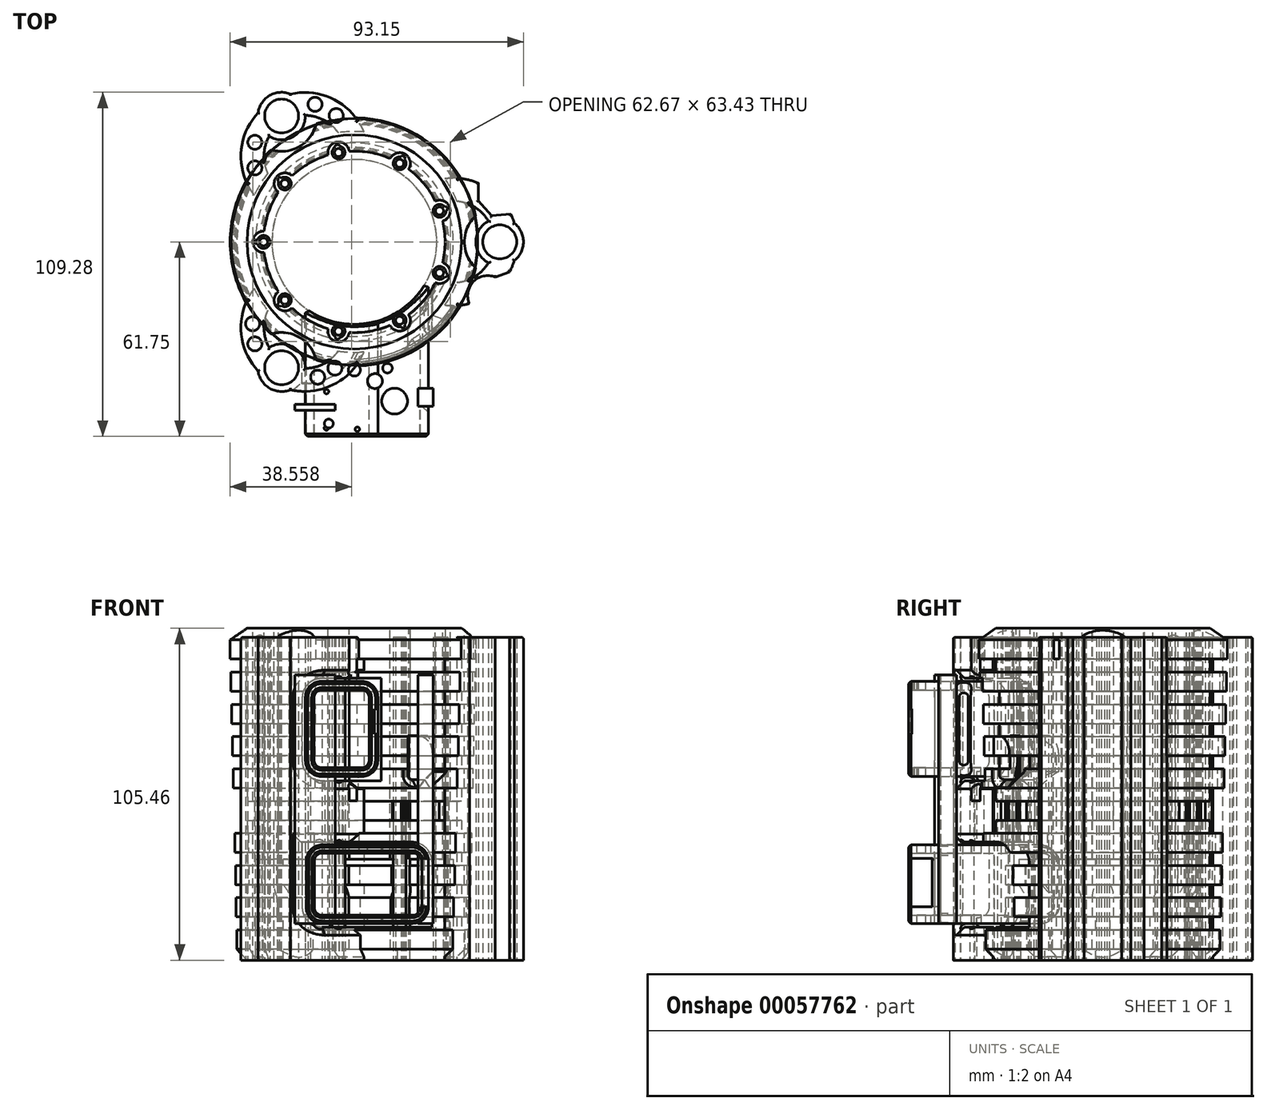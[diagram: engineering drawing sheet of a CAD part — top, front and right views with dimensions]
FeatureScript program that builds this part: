
annotation { "Feature Type Name" : "Feature", "Feature Type Description" : "" }
export const myFeature = defineFeature(function(context is Context, id is Id, definition is map)
    precondition{}
    {
        {
            var Q0;
            Q0=qCreatedBy(makeId("Front.planeOp"),FACE);
            var sketch = newSketch(context, id + "F0", { "sketchPlane" : qUnion([Q0])});
            skLineSegment(sketch, "E0.bottom", {"start": v(28.82, 39.62) * mm, "end": v(34.03, 39.62) * mm});
            skLineSegment(sketch, "E0.top", {"start": v(28.82, -33.71) * mm, "end": v(31.42, -33.71) * mm});
            skLineSegment(sketch, "E0.left", {"start": v(28.82, 39.62) * mm, "end": v(28.82, -33.71) * mm});
            skLineSegment(sketch, "E1.top", {"start": v(34.03, 29.82) * mm, "end": v(39.43, 29.82) * mm});
            skLineSegment(sketch, "E1.right", {"start": v(39.43, 35.92) * mm, "end": v(39.43, 29.82) * mm});
            skLineSegment(sketch, "E2.1.0.0", {"start": v(34.03, 25.68) * mm, "end": v(39.19, 25.68) * mm});
            skLineSegment(sketch, "E2.1.0.1", {"start": v(39.19, 25.68) * mm, "end": v(39.19, 19.58) * mm});
            skLineSegment(sketch, "E2.1.0.2", {"start": v(34.03, 19.58) * mm, "end": v(39.19, 19.58) * mm});
            skLineSegment(sketch, "E2.2.0.0", {"start": v(34.03, 15.44) * mm, "end": v(38.95, 15.44) * mm});
            skLineSegment(sketch, "E2.2.0.1", {"start": v(38.95, 15.44) * mm, "end": v(38.95, 9.34) * mm});
            skLineSegment(sketch, "E2.2.0.2", {"start": v(34.03, 9.34) * mm, "end": v(38.95, 9.34) * mm});
            skLineSegment(sketch, "E2.3.0.0", {"start": v(34.03, 5.2) * mm, "end": v(38.7, 5.2) * mm});
            skLineSegment(sketch, "E2.3.0.1", {"start": v(38.7, 5.2) * mm, "end": v(38.7, -0.9) * mm});
            skLineSegment(sketch, "E2.3.0.2", {"start": v(34.03, -0.9) * mm, "end": v(38.7, -0.9) * mm});
            skLineSegment(sketch, "E2.4.0.0", {"start": v(34.03, -5.04) * mm, "end": v(38.47, -5.04) * mm});
            skLineSegment(sketch, "E2.4.0.1", {"start": v(38.47, -5.04) * mm, "end": v(38.47, -11.14) * mm});
            skLineSegment(sketch, "E2.4.0.2", {"start": v(34.03, -11.14) * mm, "end": v(38.47, -11.14) * mm});
            skLineSegment(sketch, "E2.5.0.0", {"start": v(30.02, -15.28) * mm, "end": v(34.03, -15.28) * mm});
            skLineSegment(sketch, "E2.5.0.2", {"start": v(30.02, -21.38) * mm, "end": v(34.03, -21.38) * mm});
            skLineSegment(sketch, "E2.5.0.3", {"start": v(30.02, -15.28) * mm, "end": v(30.02, -21.38) * mm});
            skLineSegment(sketch, "E2.6.0.0", {"start": v(34.03, -25.52) * mm, "end": v(38, -25.52) * mm});
            skLineSegment(sketch, "E2.6.0.1", {"start": v(38, -25.52) * mm, "end": v(38, -31.62) * mm});
            skLineSegment(sketch, "E2.6.0.2", {"start": v(34.03, -31.62) * mm, "end": v(38, -31.62) * mm});
            skLineSegment(sketch, "E2.7.0.0", {"start": v(29.54, -35.76) * mm, "end": v(31.42, -35.76) * mm});
            skLineSegment(sketch, "E2.7.0.1", {"start": v(37.75, -35.76) * mm, "end": v(37.75, -41.86) * mm});
            skLineSegment(sketch, "E2.7.0.2", {"start": v(29.54, -41.86) * mm, "end": v(31.42, -41.86) * mm});
            skLineSegment(sketch, "E2.7.0.3", {"start": v(29.54, -35.76) * mm, "end": v(29.54, -41.86) * mm});
            skLineSegment(sketch, "E2.8.0.1", {"start": v(37.52, -46) * mm, "end": v(37.52, -52.1) * mm});
            skLineSegment(sketch, "E2.8.0.2", {"start": v(29.3, -52.1) * mm, "end": v(31.42, -52.1) * mm});
            skLineSegment(sketch, "E2.8.0.3", {"start": v(29.3, -46) * mm, "end": v(29.3, -52.1) * mm});
            skLineSegment(sketch, "E2.9.0.0", {"start": v(29.07, -56.24) * mm, "end": v(31.42, -56.24) * mm});
            skLineSegment(sketch, "E2.9.0.1", {"start": v(37.28, -56.24) * mm, "end": v(37.28, -62.34) * mm});
            skLineSegment(sketch, "E2.9.0.2", {"start": v(29.07, -62.34) * mm, "end": v(31.42, -62.34) * mm});
            skLineSegment(sketch, "E2.9.0.3", {"start": v(29.07, -56.24) * mm, "end": v(29.07, -62.34) * mm});
            skLineSegment(sketch, "E3", {"start": v(39.43, 35.92) * mm, "end": v(34.03, 39.62) * mm});
            skLineSegment(sketch, "E4.trimOffspring", {"start": v(34.03, 29.82) * mm, "end": v(34.03, 25.68) * mm});
            skLineSegment(sketch, "E5.trimOffspring", {"start": v(34.03, 19.58) * mm, "end": v(34.03, 15.44) * mm});
            skLineSegment(sketch, "E6.trimOffspring", {"start": v(34.03, 9.34) * mm, "end": v(34.03, 5.2) * mm});
            skLineSegment(sketch, "E7.trimOffspring", {"start": v(34.03, -0.9) * mm, "end": v(34.03, -5.04) * mm});
            skLineSegment(sketch, "E8.trimOffspring", {"start": v(34.03, -11.14) * mm, "end": v(34.03, -15.28) * mm});
            skLineSegment(sketch, "E9.trimOffspring", {"start": v(34.03, -21.38) * mm, "end": v(34.03, -25.52) * mm});
            skLineSegment(sketch, "E10.trimOffspring", {"start": v(34.03, -31.62) * mm, "end": v(34.03, -33.71) * mm});
            skPoint(sketch, "E11.firstSnap0", {"position": v(31.42, -33.71) * mm});
            skLineSegment(sketch, "E11.top", {"start": v(31.42, -65.84) * mm, "end": v(34.03, -65.84) * mm});
            skLineSegment(sketch, "E11.left", {"start": v(31.42, -33.71) * mm, "end": v(31.42, -35.76) * mm});
            skLineSegment(sketch, "E11.right", {"start": v(34.03, -31.62) * mm, "end": v(34.03, -35.76) * mm});
            skPoint(sketch, "E12.orphan", {"position": v(31.42, -31.62) * mm});
            skLineSegment(sketch, "E13.trimOffspring", {"start": v(34.03, -35.76) * mm, "end": v(37.75, -35.76) * mm});
            skLineSegment(sketch, "E14.trimOffspring", {"start": v(34.03, -41.86) * mm, "end": v(34.03, -46) * mm});
            skLineSegment(sketch, "E15.trimOffspring", {"start": v(31.42, -52.1) * mm, "end": v(31.42, -56.24) * mm});
            skLineSegment(sketch, "E16.trimOffspring", {"start": v(34.03, -52.1) * mm, "end": v(34.03, -56.24) * mm});
            skLineSegment(sketch, "E17.trimOffspring", {"start": v(31.42, -62.34) * mm, "end": v(31.42, -65.84) * mm});
            skLineSegment(sketch, "E18.trimOffspring", {"start": v(34.03, -56.24) * mm, "end": v(37.28, -56.24) * mm});
            skLineSegment(sketch, "E19.trimOffspring", {"start": v(34.03, -52.1) * mm, "end": v(37.52, -52.1) * mm});
            skLineSegment(sketch, "E20.trimOffspring", {"start": v(34.03, -46) * mm, "end": v(37.52, -46) * mm});
            skLineSegment(sketch, "E21.trimOffspring", {"start": v(34.03, -41.86) * mm, "end": v(37.75, -41.86) * mm});
            skLineSegment(sketch, "E22", {"start": v(34.03, -65.84) * mm, "end": v(37.28, -62.34) * mm});
            skLineSegment(sketch, "E23", {"start": v(29.3, -46) * mm, "end": v(31.42, -41.86) * mm});
            skPoint(sketch, "E24", {"position": v(0, 0) * mm});
            skLineSegment(sketch, "E25", {"start": v(0, 0) * mm, "end": v(0, 23.52) * mm});
            skSolve(sketch);
        }
        {
            var Q0;
            Q0=makeQuery(id+"F0.imprint","IMPRINT",FACE,{"disambiguationData":[TD([[makeQuery(id+"F0.imprint","IMPRINT",EDGE,{"derivedFrom":sQuery(id+"F0.wireOp",EDGE,"E0.bottom")}),-1.0]])]});
            var Q1;
            Q1=sQuery(id+"F0.wireOp",EDGE,"E25");
            revolve(context, id + "F1", {"entities" : qUnion([Q0]), "axis" : qUnion([Q1]), "revolveType" : RevolveType.FULL});
        }
        {
            var Q0;
            Q0=makeQuery(id+"F1.opRevolve","SWEPT_FACE",FACE,{"disambiguationData":[OSD([sQuery(id+"F0.wireOp",EDGE,"E0.bottom")])]});
            var sketch = newSketch(context, id + "F2", { "sketchPlane" : qUnion([Q0])});
            skCircle(sketch, "E26", {"center": v(46.18, 0) * mm, "radius": 11.2 * mm});
            skCircle(sketch, "E27.1.0", {"center": v(-23.09, 39.99) * mm, "radius": 11.2 * mm});
            skCircle(sketch, "E27.2.0", {"center": v(-23.09, -39.99) * mm, "radius": 11.2 * mm});
            skPoint(sketch, "E27.center", {"position": v(0, 0) * mm});
            skCircle(sketch, "E28", {"center": v(-28.82, 0) * mm, "radius": 3.4 * mm});
            skCircle(sketch, "E29.1.0", {"center": v(-22.07, -18.52) * mm, "radius": 3.4 * mm});
            skCircle(sketch, "E29.2.0", {"center": v(-5, -28.38) * mm, "radius": 3.4 * mm});
            skCircle(sketch, "E29.3.0", {"center": v(14.4, -24.95) * mm, "radius": 3.4 * mm});
            skCircle(sketch, "E29.4.0", {"center": v(27.08, -9.86) * mm, "radius": 3.4 * mm});
            skCircle(sketch, "E29.5.0", {"center": v(27.08, 9.86) * mm, "radius": 3.4 * mm});
            skCircle(sketch, "E29.6.0", {"center": v(14.4, 24.95) * mm, "radius": 3.4 * mm});
            skCircle(sketch, "E29.7.0", {"center": v(-5, 28.38) * mm, "radius": 3.4 * mm});
            skCircle(sketch, "E29.8.0", {"center": v(-22.07, 18.52) * mm, "radius": 3.4 * mm});
            skSolve(sketch);
        }
        {
            var Q0;
            Q0=makeQuery(id+"F1.opRevolve","SWEPT_FACE",FACE,{"disambiguationData":[OSD([sQuery(id+"F0.wireOp",EDGE,"E11.top")])]});
            var sketch = newSketch(context, id + "F3", { "sketchPlane" : qUnion([Q0])});
            skCircle(sketch, "E30", {"center": v(46.18, 0) * mm, "radius": 5.4 * mm});
            skPoint(sketch, "E31.center", {"position": v(0, 0) * mm});
            skArc(sketch, "E32", {"start": v(-30.81, -0.54) * mm, "mid": v(-26.75, -0.02) * mm, "end": v(-30.8, 0.58) * mm});
            skCircle(sketch, "E33.0", {"center": v(-28.82, 0) * mm, "radius": 1.27 * mm});
            skLineSegment(sketch, "E34.bottom", {"start": v(-30.8, 0.58) * mm, "end": v(-32.97, 0.58) * mm});
            skLineSegment(sketch, "E34.top", {"start": v(-30.81, -0.54) * mm, "end": v(-32.97, -0.54) * mm});
            skLineSegment(sketch, "E34.right", {"start": v(-32.97, 0.58) * mm, "end": v(-32.97, -0.54) * mm});
            skArc(sketch, "E35.1.0", {"start": v(-23.25, -20.22) * mm, "mid": v(-20.48, -17.2) * mm, "end": v(-23.97, -19.35) * mm});
            skLineSegment(sketch, "E35.1.1", {"start": v(-23.25, -20.22) * mm, "end": v(-24.9, -21.6) * mm});
            skLineSegment(sketch, "E35.1.2", {"start": v(-23.97, -19.35) * mm, "end": v(-25.63, -20.74) * mm});
            skCircle(sketch, "E35.1.3", {"center": v(-22.07, -18.52) * mm, "radius": 1.27 * mm});
            skLineSegment(sketch, "E35.1.4", {"start": v(-25.63, -20.74) * mm, "end": v(-24.9, -21.6) * mm});
            skArc(sketch, "E35.2.0", {"start": v(-4.82, -30.44) * mm, "mid": v(-4.62, -26.34) * mm, "end": v(-5.92, -30.23) * mm});
            skLineSegment(sketch, "E35.2.1", {"start": v(-4.82, -30.44) * mm, "end": v(-5.2, -32.56) * mm});
            skLineSegment(sketch, "E35.2.2", {"start": v(-5.92, -30.23) * mm, "end": v(-6.3, -32.36) * mm});
            skCircle(sketch, "E35.2.3", {"center": v(-5, -28.38) * mm, "radius": 1.27 * mm});
            skLineSegment(sketch, "E35.2.4", {"start": v(-6.3, -32.36) * mm, "end": v(-5.2, -32.56) * mm});
            skArc(sketch, "E36.2.3.0", {"start": v(15.87, -26.41) * mm, "mid": v(13.4, -23.15) * mm, "end": v(14.9, -26.96) * mm});
            skLineSegment(sketch, "E36.4.3.0", {"start": v(15.87, -26.41) * mm, "end": v(16.95, -28.28) * mm});
            skLineSegment(sketch, "E36.7.3.0", {"start": v(14.9, -26.96) * mm, "end": v(15.98, -28.84) * mm});
            skCircle(sketch, "E36.10.3.0", {"center": v(14.4, -24.95) * mm, "radius": 1.27 * mm});
            skLineSegment(sketch, "E36.12.3.0", {"start": v(15.98, -28.84) * mm, "end": v(16.95, -28.28) * mm});
            skArc(sketch, "E36.2.4.0", {"start": v(29.14, -10.03) * mm, "mid": v(25.14, -9.13) * mm, "end": v(28.74, -11.08) * mm});
            skLineSegment(sketch, "E36.4.4.0", {"start": v(29.14, -10.03) * mm, "end": v(31.16, -10.77) * mm});
            skLineSegment(sketch, "E36.7.4.0", {"start": v(28.74, -11.08) * mm, "end": v(30.78, -11.82) * mm});
            skCircle(sketch, "E36.10.4.0", {"center": v(27.08, -9.86) * mm, "radius": 1.27 * mm});
            skLineSegment(sketch, "E36.12.4.0", {"start": v(30.78, -11.82) * mm, "end": v(31.16, -10.77) * mm});
            skArc(sketch, "E36.2.5.0", {"start": v(28.77, 11.05) * mm, "mid": v(25.13, 9.17) * mm, "end": v(29.14, 9.99) * mm});
            skLineSegment(sketch, "E36.4.5.0", {"start": v(28.77, 11.05) * mm, "end": v(30.8, 11.78) * mm});
            skLineSegment(sketch, "E36.7.5.0", {"start": v(29.14, 9.99) * mm, "end": v(31.18, 10.73) * mm});
            skCircle(sketch, "E36.10.5.0", {"center": v(27.08, 9.86) * mm, "radius": 1.27 * mm});
            skLineSegment(sketch, "E36.12.5.0", {"start": v(31.18, 10.73) * mm, "end": v(30.8, 11.78) * mm});
            skArc(sketch, "E36.2.6.0", {"start": v(14.94, 26.95) * mm, "mid": v(13.36, 23.17) * mm, "end": v(15.9, 26.38) * mm});
            skLineSegment(sketch, "E36.4.6.0", {"start": v(14.94, 26.95) * mm, "end": v(16.01, 28.82) * mm});
            skLineSegment(sketch, "E36.7.6.0", {"start": v(15.9, 26.38) * mm, "end": v(16.99, 28.26) * mm});
            skCircle(sketch, "E36.10.6.0", {"center": v(14.4, 24.95) * mm, "radius": 1.27 * mm});
            skLineSegment(sketch, "E36.12.6.0", {"start": v(16.99, 28.26) * mm, "end": v(16.01, 28.82) * mm});
            skArc(sketch, "E36.2.7.0", {"start": v(-5.88, 30.25) * mm, "mid": v(-4.67, 26.34) * mm, "end": v(-4.78, 30.43) * mm});
            skLineSegment(sketch, "E36.4.7.0", {"start": v(-5.88, 30.25) * mm, "end": v(-6.26, 32.37) * mm});
            skLineSegment(sketch, "E36.7.7.0", {"start": v(-4.78, 30.43) * mm, "end": v(-5.15, 32.57) * mm});
            skCircle(sketch, "E36.10.7.0", {"center": v(-5, 28.38) * mm, "radius": 1.27 * mm});
            skLineSegment(sketch, "E36.12.7.0", {"start": v(-5.15, 32.57) * mm, "end": v(-6.26, 32.37) * mm});
            skArc(sketch, "E36.2.8.0", {"start": v(-23.95, 19.4) * mm, "mid": v(-20.5, 17.18) * mm, "end": v(-23.22, 20.24) * mm});
            skLineSegment(sketch, "E36.4.8.0", {"start": v(-23.95, 19.4) * mm, "end": v(-25.6, 20.77) * mm});
            skLineSegment(sketch, "E36.7.8.0", {"start": v(-23.22, 20.24) * mm, "end": v(-24.88, 21.64) * mm});
            skCircle(sketch, "E36.10.8.0", {"center": v(-22.07, 18.52) * mm, "radius": 1.27 * mm});
            skLineSegment(sketch, "E36.12.8.0", {"start": v(-24.88, 21.64) * mm, "end": v(-25.6, 20.77) * mm});
            skCircle(sketch, "E37.0", {"center": v(46.18, 0) * mm, "radius": 7.54 * mm});
            skArc(sketch, "E38", {"start": v(28.73, -20.1) * mm, "mid": v(34.18, -20.1) * mm, "end": v(39.43, -18.64) * mm});
            skArc(sketch, "E39", {"start": v(32.6, -12.92) * mm, "mid": v(38.35, -10.98) * mm, "end": v(42.58, -6.63) * mm});
            skArc(sketch, "E40", {"start": v(28.73, -20.1) * mm, "mid": v(30.88, -16.63) * mm, "end": v(32.6, -12.92) * mm});
            skArc(sketch, "E41.trimOffspring", {"start": v(32.6, 12.92) * mm, "mid": v(30.88, 16.63) * mm, "end": v(28.73, 20.1) * mm});
            skArc(sketch, "E42.trimOffspring", {"start": v(42.58, 6.63) * mm, "mid": v(38.35, 10.98) * mm, "end": v(32.6, 12.92) * mm});
            skArc(sketch, "E43.trimOffspring", {"start": v(50.82, 5.94) * mm, "mid": v(50.15, 7.8) * mm, "end": v(49.3, 9.58) * mm});
            skCircle(sketch, "E44.1.0", {"center": v(-23.09, 39.99) * mm, "radius": 7.54 * mm});
            skCircle(sketch, "E44.1.1", {"center": v(-23.09, 39.99) * mm, "radius": 5.4 * mm});
            skArc(sketch, "E44.1.2", {"start": v(-27.03, 33.56) * mm, "mid": v(-28.68, 27.72) * mm, "end": v(-27.5, 21.77) * mm});
            skArc(sketch, "E44.1.3", {"start": v(-30.56, 41.04) * mm, "mid": v(-35.98, 28.16) * mm, "end": v(-31.78, 14.83) * mm});
            skArc(sketch, "E44.1.4", {"start": v(-27.5, 21.77) * mm, "mid": v(-29.84, 18.43) * mm, "end": v(-31.78, 14.83) * mm});
            skArc(sketch, "E44.1.5", {"start": v(3.05, 34.94) * mm, "mid": v(-1.04, 35.05) * mm, "end": v(-5.1, 34.7) * mm});
            skArc(sketch, "E44.1.6", {"start": v(-5.1, 34.7) * mm, "mid": v(-9.67, 38.7) * mm, "end": v(-15.55, 40.2) * mm});
            skArc(sketch, "E44.1.7", {"start": v(3.05, 34.94) * mm, "mid": v(-6.4, 45.24) * mm, "end": v(-20.26, 46.98) * mm});
            skCircle(sketch, "E44.2.0", {"center": v(-23.09, -39.99) * mm, "radius": 7.54 * mm});
            skCircle(sketch, "E44.2.1", {"center": v(-23.09, -39.99) * mm, "radius": 5.4 * mm});
            skArc(sketch, "E44.2.2", {"start": v(-15.55, -40.2) * mm, "mid": v(-9.67, -38.7) * mm, "end": v(-5.1, -34.7) * mm});
            skArc(sketch, "E44.2.3", {"start": v(-20.26, -46.98) * mm, "mid": v(-6.4, -45.24) * mm, "end": v(3.05, -34.94) * mm});
            skArc(sketch, "E44.2.4", {"start": v(-5.1, -34.7) * mm, "mid": v(-1.04, -35.05) * mm, "end": v(3.05, -34.94) * mm});
            skArc(sketch, "E44.2.5", {"start": v(-31.78, -14.83) * mm, "mid": v(-29.84, -18.43) * mm, "end": v(-27.5, -21.77) * mm});
            skArc(sketch, "E44.2.6", {"start": v(-27.5, -21.77) * mm, "mid": v(-28.68, -27.72) * mm, "end": v(-27.03, -33.56) * mm});
            skArc(sketch, "E44.2.7", {"start": v(-31.78, -14.83) * mm, "mid": v(-35.98, -28.16) * mm, "end": v(-30.56, -41.04) * mm});
            skLineSegment(sketch, "E45", {"start": v(39.43, -18.64) * mm, "end": v(39.43, -13.03) * mm});
            skLineSegment(sketch, "E46", {"start": v(39.43, -13.03) * mm, "end": v(43.6, -8.36) * mm});
            skLineSegment(sketch, "E47", {"start": v(43.6, -8.36) * mm, "end": v(49.7, -8.83) * mm});
            skArc(sketch, "E48.trimOffspring", {"start": v(49.7, -8.83) * mm, "mid": v(50.31, -7.4) * mm, "end": v(50.82, -5.94) * mm});
            skArc(sketch, "E49", {"start": v(36.56, 19.62) * mm, "mid": v(37.8, 12.67) * mm, "end": v(44.7, 11.17) * mm});
            skArc(sketch, "E50.trimOffspring", {"start": v(36.56, 19.62) * mm, "mid": v(32.67, 20.25) * mm, "end": v(28.73, 20.1) * mm});
            skLineSegment(sketch, "E51", {"start": v(44.7, 11.17) * mm, "end": v(49.3, 9.58) * mm});
            skSolve(sketch);
        }
        {
            var Q0;
            Q0 = qSketchRegion(id + "F2", true);
            extrude(context, id + "F4", {"entities" : qUnion([Q0]), "operationType" : NewBodyOperationType.REMOVE, "oppositeDirection" : true, "depth" : 120.19 * mm});
        }
        {
            var Q0;
            Q0=makeQuery(id+"F3.imprint","IMPRINT",FACE,{"disambiguationData":[TD([[makeQuery(id+"F3.imprint","IMPRINT",EDGE,{"derivedFrom":sQuery(id+"F3.wireOp",EDGE,"E41.trimOffspring")}),-1.0]])]});
            var Q1;
            {var subQ0=sQuery(id+"F3.wireOp",EDGE,"E38");Q1=makeQuery(id+"F3.imprint","IMPRINT",FACE,{"disambiguationData":[TD([[makeQuery(id+"F3.imprint","IMPRINT",EDGE,{"derivedFrom":subQ0}),1.0]])]});}
            var Q2;
            Q2=makeQuery(id+"F3.imprint","IMPRINT",FACE,{"disambiguationData":[TD([[makeQuery(id+"F3.imprint","IMPRINT",EDGE,{"derivedFrom":sQuery(id+"F3.wireOp",EDGE,"E30")}),-1.0]])]});
            var Q3;
            {var subQ0=sQuery(id+"F3.wireOp",EDGE,"E44.2.2");Q3=makeQuery(id+"F3.imprint","IMPRINT",FACE,{"disambiguationData":[TD([[makeQuery(id+"F3.imprint","IMPRINT",EDGE,{"derivedFrom":subQ0}),-1.0]])]});}
            var Q4;
            Q4=makeQuery(id+"F3.imprint","IMPRINT",FACE,{"disambiguationData":[TD([[makeQuery(id+"F3.imprint","IMPRINT",EDGE,{"derivedFrom":sQuery(id+"F3.wireOp",EDGE,"E44.2.5")}),-1.0]])]});
            var Q5;
            Q5=makeQuery(id+"F3.imprint","IMPRINT",FACE,{"disambiguationData":[TD([[makeQuery(id+"F3.imprint","IMPRINT",EDGE,{"derivedFrom":sQuery(id+"F3.wireOp",EDGE,"E44.2.1")}),-1.0]])]});
            var Q6;
            Q6=makeQuery(id+"F3.imprint","IMPRINT",FACE,{"disambiguationData":[TD([[makeQuery(id+"F3.imprint","IMPRINT",EDGE,{"derivedFrom":sQuery(id+"F3.wireOp",EDGE,"E44.1.5")}),-1.0]])]});
            var Q7;
            {var subQ0=sQuery(id+"F3.wireOp",EDGE,"E44.1.2");Q7=makeQuery(id+"F3.imprint","IMPRINT",FACE,{"disambiguationData":[TD([[makeQuery(id+"F3.imprint","IMPRINT",EDGE,{"derivedFrom":subQ0}),-1.0]])]});}
            var Q8;
            Q8=makeQuery(id+"F3.imprint","IMPRINT",FACE,{"disambiguationData":[TD([[makeQuery(id+"F3.imprint","IMPRINT",EDGE,{"derivedFrom":sQuery(id+"F3.wireOp",EDGE,"E44.1.1")}),-1.0]])]});
            var Q9;
            {var subQ1=sQuery(id+"F3.wireOp",EDGE,"E35.2.0");Q9=makeQuery(id+"F3.imprint","IMPRINT",FACE,{"disambiguationData":[TD([[makeQuery(id+"F3.imprint","IMPRINT",EDGE,{"derivedFrom":subQ1}),1.0]])]});}
            var Q10;
            {var subQ1=sQuery(id+"F3.wireOp",EDGE,"E35.1.0");Q10=makeQuery(id+"F3.imprint","IMPRINT",FACE,{"disambiguationData":[TD([[makeQuery(id+"F3.imprint","IMPRINT",EDGE,{"derivedFrom":subQ1}),1.0]])]});}
            var Q11;
            {var subQ1=sQuery(id+"F3.wireOp",EDGE,"E32");Q11=makeQuery(id+"F3.imprint","IMPRINT",FACE,{"disambiguationData":[TD([[makeQuery(id+"F3.imprint","IMPRINT",EDGE,{"derivedFrom":subQ1}),1.0]])]});}
            var Q12;
            {var subQ1=sQuery(id+"F3.wireOp",EDGE,"E36.2.8.0");Q12=makeQuery(id+"F3.imprint","IMPRINT",FACE,{"disambiguationData":[TD([[makeQuery(id+"F3.imprint","IMPRINT",EDGE,{"derivedFrom":subQ1}),1.0]])]});}
            var Q13;
            {var subQ5=sQuery(id+"F3.wireOp",EDGE,"E36.2.7.0");Q13=makeQuery(id+"F3.imprint","IMPRINT",FACE,{"disambiguationData":[TD([[makeQuery(id+"F3.imprint","IMPRINT",EDGE,{"derivedFrom":subQ5}),1.0]])]});}
            var Q14;
            {var subQ1=sQuery(id+"F3.wireOp",EDGE,"E36.2.6.0");Q14=makeQuery(id+"F3.imprint","IMPRINT",FACE,{"disambiguationData":[TD([[makeQuery(id+"F3.imprint","IMPRINT",EDGE,{"derivedFrom":subQ1}),1.0]])]});}
            var Q15;
            {var subQ1=sQuery(id+"F3.wireOp",EDGE,"E36.2.5.0");Q15=makeQuery(id+"F3.imprint","IMPRINT",FACE,{"disambiguationData":[TD([[makeQuery(id+"F3.imprint","IMPRINT",EDGE,{"derivedFrom":subQ1}),1.0]])]});}
            var Q16;
            {var subQ1=sQuery(id+"F3.wireOp",EDGE,"E36.2.4.0");Q16=makeQuery(id+"F3.imprint","IMPRINT",FACE,{"disambiguationData":[TD([[makeQuery(id+"F3.imprint","IMPRINT",EDGE,{"derivedFrom":subQ1}),1.0]])]});}
            var Q17;
            {var subQ1=sQuery(id+"F3.wireOp",EDGE,"E36.2.3.0");Q17=makeQuery(id+"F3.imprint","IMPRINT",FACE,{"disambiguationData":[TD([[makeQuery(id+"F3.imprint","IMPRINT",EDGE,{"derivedFrom":subQ1}),1.0]])]});}
            extrude(context, id + "F5", {"entities" : qUnion([Q0, Q1, Q2, Q3, Q4, Q5, Q6, Q7, Q8, Q9, Q10, Q11, Q12, Q13, Q14, Q15, Q16, Q17]), "operationType" : NewBodyOperationType.ADD, "oppositeDirection" : true, "depth" : 102.53 * mm});
        }
        {
            var Q0;
            Q0=makeQuery(id+"F5.opExtrude","CAP_FACE",FACE,{"disambiguationData":[OSD([sQuery(id+"F3.wireOp",EDGE,"E44.2.0"),sQuery(id+"F3.wireOp",EDGE,"E44.2.1"),sQuery(id+"F3.wireOp",EDGE,"E44.2.2"),sQuery(id+"F3.wireOp",EDGE,"E44.2.3"),sQuery(id+"F3.wireOp",EDGE,"E44.2.4"),sQuery(id+"F3.wireOp",EDGE,"E44.2.5"),sQuery(id+"F3.wireOp",EDGE,"E44.2.6"),sQuery(id+"F3.wireOp",EDGE,"E44.2.7")])],"isStart":false});
            var Q1;
            Q1=makeQuery(id+"F5.opExtrude","CAP_FACE",FACE,{"disambiguationData":[OSD([sQuery(id+"F3.wireOp",EDGE,"E44.1.0"),sQuery(id+"F3.wireOp",EDGE,"E44.1.1"),sQuery(id+"F3.wireOp",EDGE,"E44.1.2"),sQuery(id+"F3.wireOp",EDGE,"E44.1.3"),sQuery(id+"F3.wireOp",EDGE,"E44.1.4"),sQuery(id+"F3.wireOp",EDGE,"E44.1.5"),sQuery(id+"F3.wireOp",EDGE,"E44.1.6"),sQuery(id+"F3.wireOp",EDGE,"E44.1.7")])],"isStart":false});
            var Q2;
            Q2=makeQuery(id+"F5.opExtrude","CAP_FACE",FACE,{"disambiguationData":[OSD([sQuery(id+"F3.wireOp",EDGE,"E30"),sQuery(id+"F3.wireOp",EDGE,"E37.0"),sQuery(id+"F3.wireOp",EDGE,"E38"),sQuery(id+"F3.wireOp",EDGE,"E39"),sQuery(id+"F3.wireOp",EDGE,"E40"),sQuery(id+"F3.wireOp",EDGE,"E41.trimOffspring"),sQuery(id+"F3.wireOp",EDGE,"E42.trimOffspring"),sQuery(id+"F3.wireOp",EDGE,"E43.trimOffspring"),sQuery(id+"F3.wireOp",EDGE,"E45"),sQuery(id+"F3.wireOp",EDGE,"E46"),sQuery(id+"F3.wireOp",EDGE,"E47"),sQuery(id+"F3.wireOp",EDGE,"E48.trimOffspring")])],"isStart":false});
            fillet(context, id + "F6", {"entities" : qUnion([Q0, Q1, Q2]), "radius" : 0.5 * mm, "tangentPropagation" : true, "allowEdgeOverflow" : false});
        }
        {
            var Q0;
            Q0=qCreatedBy(makeId("Front.planeOp"),FACE);
            var sketch = newSketch(context, id + "F7", { "sketchPlane" : qUnion([Q0])});
            skLineSegment(sketch, "E52.bottom", {"start": v(-10.2, -55.34) * mm, "end": v(24.69, -55.34) * mm});
            skLineSegment(sketch, "E52.top", {"start": v(-16.55, -28.34) * mm, "end": v(18.34, -28.34) * mm});
            skLineSegment(sketch, "E52.left", {"start": v(-16.55, -48.99) * mm, "end": v(-16.55, -28.34) * mm});
            skLineSegment(sketch, "E52.right", {"start": v(24.69, -55.34) * mm, "end": v(24.69, -34.7) * mm});
            skLineSegment(sketch, "E53.bottom", {"start": v(-10.2, -8.85) * mm, "end": v(8.56, -8.85) * mm});
            skLineSegment(sketch, "E53.top", {"start": v(-10.2, 23.77) * mm, "end": v(8.56, 23.77) * mm});
            skLineSegment(sketch, "E53.left", {"start": v(-16.55, -2.5) * mm, "end": v(-16.55, 17.42) * mm});
            skLineSegment(sketch, "E53.right", {"start": v(8.56, -8.85) * mm, "end": v(8.56, 23.77) * mm});
            skLineSegment(sketch, "E54.bottom", {"start": v(18.39, -8.47) * mm, "end": v(24.82, -8.47) * mm});
            skLineSegment(sketch, "E54.top", {"start": v(17.05, 5.5) * mm, "end": v(21.04, 5.5) * mm});
            skLineSegment(sketch, "E54.left", {"start": v(17.05, -7.13) * mm, "end": v(17.05, 5.5) * mm});
            skLineSegment(sketch, "E54.right", {"start": v(24.82, -8.47) * mm, "end": v(24.82, 0) * mm});
            skPoint(sketch, "E55.visualSharp", {"position": v(-16.55, -55.34) * mm});
            skArc(sketch, "E55.filletArc", {"start": v(-16.55, -48.99) * mm, "mid": v(-14.7, -53.48) * mm, "end": v(-10.2, -55.34) * mm});
            skPoint(sketch, "E56.visualSharp", {"position": v(24.69, -28.34) * mm});
            skArc(sketch, "E56.filletArc", {"start": v(24.69, -34.7) * mm, "mid": v(22.83, -30.2) * mm, "end": v(18.34, -28.34) * mm});
            skPoint(sketch, "E57.visualSharp", {"position": v(-16.55, -8.85) * mm});
            skArc(sketch, "E57.filletArc", {"start": v(-16.55, -2.5) * mm, "mid": v(-14.7, -6.99) * mm, "end": v(-10.2, -8.85) * mm});
            skPoint(sketch, "E58.visualSharp", {"position": v(-16.55, 23.77) * mm});
            skArc(sketch, "E58.filletArc", {"start": v(-10.2, 23.77) * mm, "mid": v(-14.7, 21.91) * mm, "end": v(-16.55, 17.42) * mm});
            skArc(sketch, "E59.filletArc", {"start": v(24.82, 0) * mm, "mid": v(23.79, 3.33) * mm, "end": v(21.04, 5.5) * mm});
            skPoint(sketch, "E60.visualSharp", {"position": v(17.19, -8.47) * mm});
            skArc(sketch, "E60.filletArc", {"start": v(17.05, -7.13) * mm, "mid": v(17.44, -8.08) * mm, "end": v(18.39, -8.47) * mm});
            skSolve(sketch);
        }
        {
            var Q0;
            Q0 = qSketchRegion(id + "F7", true);
            extrude(context, id + "F8", {"entities" : qUnion([Q0]), "operationType" : NewBodyOperationType.REMOVE, "depth" : 93.07 * mm});
        }
        {
            var Q0;
            Q0=makeQuery(id+"F8.boolean.opBoolean","INTERSECT",EDGE,{"derivedFrom":[makeQuery(id+"F5.opExtrude","SWEPT_FACE",FACE,{"disambiguationData":[OSD([sQuery(id+"F3.wireOp",EDGE,"E44.1.7")])]}),makeQuery(id+"F8.opExtrude","SWEPT_FACE",FACE,{"disambiguationData":[OSD([sQuery(id+"F7.wireOp",EDGE,"E53.left")])]})]});
            var Q1;
            Q1=makeQuery(id+"F8.boolean.opBoolean","INTERSECT",EDGE,{"derivedFrom":[makeQuery(id+"F5.opExtrude","SWEPT_FACE",FACE,{"disambiguationData":[OSD([sQuery(id+"F3.wireOp",EDGE,"E44.1.7")])]}),makeQuery(id+"F8.opExtrude","SWEPT_FACE",FACE,{"disambiguationData":[OSD([sQuery(id+"F7.wireOp",EDGE,"E58.filletArc")])]})]});
            var Q2;
            Q2=makeQuery(id+"F8.boolean.opBoolean","INTERSECT",EDGE,{"derivedFrom":[makeQuery(id+"F5.opExtrude","SWEPT_FACE",FACE,{"disambiguationData":[OSD([sQuery(id+"F3.wireOp",EDGE,"E44.1.7")])]}),makeQuery(id+"F8.opExtrude","SWEPT_FACE",FACE,{"disambiguationData":[OSD([sQuery(id+"F7.wireOp",EDGE,"E53.top")])]})]});
            var Q3;
            Q3=makeQuery(id+"F8.boolean.opBoolean","INTERSECT",EDGE,{"derivedFrom":[makeQuery(id+"F5.opExtrude","SWEPT_FACE",FACE,{"disambiguationData":[OSD([sQuery(id+"F3.wireOp",EDGE,"E44.1.7")])]}),makeQuery(id+"F8.opExtrude","SWEPT_FACE",FACE,{"disambiguationData":[OSD([sQuery(id+"F7.wireOp",EDGE,"E57.filletArc")])]})]});
            var Q4;
            Q4=makeQuery(id+"F8.boolean.opBoolean","INTERSECT",EDGE,{"derivedFrom":[makeQuery(id+"F5.opExtrude","SWEPT_FACE",FACE,{"disambiguationData":[OSD([sQuery(id+"F3.wireOp",EDGE,"E44.1.7")])]}),makeQuery(id+"F8.opExtrude","SWEPT_FACE",FACE,{"disambiguationData":[OSD([sQuery(id+"F7.wireOp",EDGE,"E53.bottom")])]})]});
            var Q5;
            Q5=makeQuery(id+"F8.boolean.opBoolean","INTERSECT",EDGE,{"derivedFrom":[makeQuery(id+"F5.opExtrude","SWEPT_FACE",FACE,{"disambiguationData":[OSD([sQuery(id+"F3.wireOp",EDGE,"E44.1.7")])]}),makeQuery(id+"F8.opExtrude","SWEPT_FACE",FACE,{"disambiguationData":[OSD([sQuery(id+"F7.wireOp",EDGE,"E52.top")])]})]});
            var Q6;
            Q6=makeQuery(id+"F8.boolean.opBoolean","INTERSECT",EDGE,{"derivedFrom":[makeQuery(id+"F5.opExtrude","SWEPT_FACE",FACE,{"disambiguationData":[OSD([sQuery(id+"F3.wireOp",EDGE,"E44.1.7")])]}),makeQuery(id+"F8.opExtrude","SWEPT_FACE",FACE,{"disambiguationData":[OSD([sQuery(id+"F7.wireOp",EDGE,"E52.left")])]})]});
            var Q7;
            Q7=makeQuery(id+"F8.boolean.opBoolean","INTERSECT",EDGE,{"derivedFrom":[makeQuery(id+"F5.opExtrude","SWEPT_FACE",FACE,{"disambiguationData":[OSD([sQuery(id+"F3.wireOp",EDGE,"E44.1.7")])]}),makeQuery(id+"F8.opExtrude","SWEPT_FACE",FACE,{"disambiguationData":[OSD([sQuery(id+"F7.wireOp",EDGE,"E55.filletArc")])]})]});
            var Q8;
            Q8=makeQuery(id+"F8.boolean.opBoolean","INTERSECT",EDGE,{"derivedFrom":[makeQuery(id+"F5.opExtrude","SWEPT_FACE",FACE,{"disambiguationData":[OSD([sQuery(id+"F3.wireOp",EDGE,"E44.1.7")])]}),makeQuery(id+"F8.opExtrude","SWEPT_FACE",FACE,{"disambiguationData":[OSD([sQuery(id+"F7.wireOp",EDGE,"E52.bottom")])]})]});
            var Q9;
            {var subQ0=makeQuery(id+"F1.opRevolve","SWEPT_FACE",FACE,{"disambiguationData":[OSD([sQuery(id+"F0.wireOp",EDGE,"E2.6.0.0")])]});var subQ1=makeQuery(id+"F1.opRevolve","SWEPT_FACE",FACE,{"disambiguationData":[OSD([sQuery(id+"F0.wireOp",EDGE,"E2.6.0.2")])]});Q9=makeQuery(id+"F8.boolean.opBoolean","INTERSECT",EDGE,{"derivedFrom":[makeQuery(id+"F5.boolean.opBoolean","SPLIT",FACE,{"disambiguationData":[TD([makeQuery(id+"F5.opExtrude","SWEPT_FACE",FACE,{"disambiguationData":[OSD([sQuery(id+"F3.wireOp",EDGE,"E43.trimOffspring")])]})])],"derivedFrom":makeQuery(id+"F4.boolean.opBoolean","SPLIT",FACE,{"disambiguationData":[TD([subQ0,subQ1,makeQuery(id+"F4.opExtrude","SWEPT_FACE",FACE,{"disambiguationData":[OSD([sQuery(id+"F2.wireOp",EDGE,"E26")])]}),makeQuery(id+"F4.opExtrude","SWEPT_FACE",FACE,{"disambiguationData":[OSD([sQuery(id+"F2.wireOp",EDGE,"E27.2.0")])]})])],"derivedFrom":makeQuery(id+"F1.opRevolve","SWEPT_FACE",FACE,{"disambiguationData":[OSD([sQuery(id+"F0.wireOp",EDGE,"E2.6.0.1")])]})})}),makeQuery(id+"F8.opExtrude","SWEPT_FACE",FACE,{"disambiguationData":[OSD([sQuery(id+"F7.wireOp",EDGE,"E52.top")])]})]});}
            var Q10;
            {var subQ0=makeQuery(id+"F1.opRevolve","SWEPT_FACE",FACE,{"disambiguationData":[OSD([sQuery(id+"F0.wireOp",EDGE,"E2.6.0.0")])]});var subQ1=makeQuery(id+"F1.opRevolve","SWEPT_FACE",FACE,{"disambiguationData":[OSD([sQuery(id+"F0.wireOp",EDGE,"E2.6.0.2")])]});Q10=makeQuery(id+"F8.boolean.opBoolean","INTERSECT",EDGE,{"derivedFrom":[makeQuery(id+"F5.boolean.opBoolean","SPLIT",FACE,{"disambiguationData":[TD([makeQuery(id+"F5.opExtrude","SWEPT_FACE",FACE,{"disambiguationData":[OSD([sQuery(id+"F3.wireOp",EDGE,"E43.trimOffspring")])]})])],"derivedFrom":makeQuery(id+"F4.boolean.opBoolean","SPLIT",FACE,{"disambiguationData":[TD([subQ0,subQ1,makeQuery(id+"F4.opExtrude","SWEPT_FACE",FACE,{"disambiguationData":[OSD([sQuery(id+"F2.wireOp",EDGE,"E26")])]}),makeQuery(id+"F4.opExtrude","SWEPT_FACE",FACE,{"disambiguationData":[OSD([sQuery(id+"F2.wireOp",EDGE,"E27.2.0")])]})])],"derivedFrom":makeQuery(id+"F1.opRevolve","SWEPT_FACE",FACE,{"disambiguationData":[OSD([sQuery(id+"F0.wireOp",EDGE,"E2.6.0.1")])]})})}),makeQuery(id+"F8.opExtrude","SWEPT_FACE",FACE,{"disambiguationData":[OSD([sQuery(id+"F7.wireOp",EDGE,"E56.filletArc")])]})]});}
            var Q11;
            {var subQ0=makeQuery(id+"F1.opRevolve","SWEPT_FACE",FACE,{"disambiguationData":[OSD([sQuery(id+"F0.wireOp",EDGE,"E13.trimOffspring")])]});var subQ1=makeQuery(id+"F1.opRevolve","SWEPT_FACE",FACE,{"disambiguationData":[OSD([sQuery(id+"F0.wireOp",EDGE,"E21.trimOffspring")])]});Q11=makeQuery(id+"F8.boolean.opBoolean","INTERSECT",EDGE,{"derivedFrom":[makeQuery(id+"F5.boolean.opBoolean","SPLIT",FACE,{"disambiguationData":[TD([makeQuery(id+"F5.opExtrude","SWEPT_FACE",FACE,{"disambiguationData":[OSD([sQuery(id+"F3.wireOp",EDGE,"E43.trimOffspring")])]})])],"derivedFrom":makeQuery(id+"F4.boolean.opBoolean","SPLIT",FACE,{"disambiguationData":[TD([subQ0,subQ1,makeQuery(id+"F4.opExtrude","SWEPT_FACE",FACE,{"disambiguationData":[OSD([sQuery(id+"F2.wireOp",EDGE,"E26")])]}),makeQuery(id+"F4.opExtrude","SWEPT_FACE",FACE,{"disambiguationData":[OSD([sQuery(id+"F2.wireOp",EDGE,"E27.2.0")])]})])],"derivedFrom":makeQuery(id+"F1.opRevolve","SWEPT_FACE",FACE,{"disambiguationData":[OSD([sQuery(id+"F0.wireOp",EDGE,"E2.7.0.1")])]})})}),makeQuery(id+"F8.opExtrude","SWEPT_FACE",FACE,{"disambiguationData":[OSD([sQuery(id+"F7.wireOp",EDGE,"E52.right")])]})]});}
            var Q12;
            {var subQ0=makeQuery(id+"F1.opRevolve","SWEPT_FACE",FACE,{"disambiguationData":[OSD([sQuery(id+"F0.wireOp",EDGE,"E2.3.0.0")])]});var subQ1=makeQuery(id+"F1.opRevolve","SWEPT_FACE",FACE,{"disambiguationData":[OSD([sQuery(id+"F0.wireOp",EDGE,"E2.3.0.2")])]});Q12=makeQuery(id+"F8.boolean.opBoolean","INTERSECT",EDGE,{"derivedFrom":[makeQuery(id+"F5.boolean.opBoolean","SPLIT",FACE,{"disambiguationData":[TD([makeQuery(id+"F5.opExtrude","SWEPT_FACE",FACE,{"disambiguationData":[OSD([sQuery(id+"F3.wireOp",EDGE,"E43.trimOffspring")])]})])],"derivedFrom":makeQuery(id+"F4.boolean.opBoolean","SPLIT",FACE,{"disambiguationData":[TD([subQ0,subQ1,makeQuery(id+"F4.opExtrude","SWEPT_FACE",FACE,{"disambiguationData":[OSD([sQuery(id+"F2.wireOp",EDGE,"E26")])]}),makeQuery(id+"F4.opExtrude","SWEPT_FACE",FACE,{"disambiguationData":[OSD([sQuery(id+"F2.wireOp",EDGE,"E27.2.0")])]})])],"derivedFrom":makeQuery(id+"F1.opRevolve","SWEPT_FACE",FACE,{"disambiguationData":[OSD([sQuery(id+"F0.wireOp",EDGE,"E2.3.0.1")])]})})}),makeQuery(id+"F8.opExtrude","SWEPT_FACE",FACE,{"disambiguationData":[OSD([sQuery(id+"F7.wireOp",EDGE,"E59.filletArc")])]})]});}
            var Q13;
            {var subQ0=makeQuery(id+"F1.opRevolve","SWEPT_FACE",FACE,{"disambiguationData":[OSD([sQuery(id+"F0.wireOp",EDGE,"E2.3.0.0")])]});var subQ1=makeQuery(id+"F1.opRevolve","SWEPT_FACE",FACE,{"disambiguationData":[OSD([sQuery(id+"F0.wireOp",EDGE,"E2.3.0.2")])]});Q13=makeQuery(id+"F8.boolean.opBoolean","INTERSECT",EDGE,{"derivedFrom":[makeQuery(id+"F5.boolean.opBoolean","SPLIT",FACE,{"disambiguationData":[TD([makeQuery(id+"F5.opExtrude","SWEPT_FACE",FACE,{"disambiguationData":[OSD([sQuery(id+"F3.wireOp",EDGE,"E43.trimOffspring")])]})])],"derivedFrom":makeQuery(id+"F4.boolean.opBoolean","SPLIT",FACE,{"disambiguationData":[TD([subQ0,subQ1,makeQuery(id+"F4.opExtrude","SWEPT_FACE",FACE,{"disambiguationData":[OSD([sQuery(id+"F2.wireOp",EDGE,"E26")])]}),makeQuery(id+"F4.opExtrude","SWEPT_FACE",FACE,{"disambiguationData":[OSD([sQuery(id+"F2.wireOp",EDGE,"E27.2.0")])]})])],"derivedFrom":makeQuery(id+"F1.opRevolve","SWEPT_FACE",FACE,{"disambiguationData":[OSD([sQuery(id+"F0.wireOp",EDGE,"E2.3.0.1")])]})})}),makeQuery(id+"F8.opExtrude","SWEPT_FACE",FACE,{"disambiguationData":[OSD([sQuery(id+"F7.wireOp",EDGE,"E54.left")])]})]});}
            var Q14;
            Q14=makeQuery(id+"F8.boolean.opBoolean","COPY",FACE,{"derivedFrom":makeQuery(id+"F8.opExtrude","SWEPT_FACE",FACE,{"disambiguationData":[OSD([sQuery(id+"F7.wireOp",EDGE,"E54.bottom")])]})});
            chamfer(context, id + "F9", {"entities" : qUnion([Q0, Q1, Q2, Q3, Q4, Q5, Q6, Q7, Q8, Q9, Q10, Q11, Q12, Q13, Q14]), "width" : 2.54 * mm, "tangentPropagation" : true});
        }
        {
            var Q0;
            Q0=makeQuery(id+"F5.opExtrude","CAP_FACE",FACE,{"disambiguationData":[OSD([sQuery(id+"F3.wireOp",EDGE,"E44.1.0"),sQuery(id+"F3.wireOp",EDGE,"E44.1.1"),sQuery(id+"F3.wireOp",EDGE,"E44.1.2"),sQuery(id+"F3.wireOp",EDGE,"E44.1.3"),sQuery(id+"F3.wireOp",EDGE,"E44.1.4"),sQuery(id+"F3.wireOp",EDGE,"E44.1.5"),sQuery(id+"F3.wireOp",EDGE,"E44.1.6"),sQuery(id+"F3.wireOp",EDGE,"E44.1.7")])],"isStart":true});
            var sketch = newSketch(context, id + "F10", { "sketchPlane" : qUnion([Q0])});
            skCircle(sketch, "E61", {"center": v(-6.16, 40.13) * mm, "radius": 2.24 * mm});
            skCircle(sketch, "E62", {"center": v(-11.65, 42.98) * mm, "radius": 2.24 * mm});
            skCircle(sketch, "E63", {"center": v(-31.6, 32.4) * mm, "radius": 2.24 * mm});
            skCircle(sketch, "E64", {"center": v(-32.3, 26.03) * mm, "radius": 2.24 * mm});
            skCircle(sketch, "E65", {"center": v(-31.6, -23.5) * mm, "radius": 2.24 * mm});
            skCircle(sketch, "E66", {"center": v(-31.6, -31.65) * mm, "radius": 2.24 * mm});
            skCircle(sketch, "E67", {"center": v(-12.48, -43.68) * mm, "radius": 2.24 * mm});
            skCircle(sketch, "E68", {"center": v(-5.76, -40.14) * mm, "radius": 2.24 * mm});
            skSolve(sketch);
        }
        {
            var Q0;
            Q0 = qSketchRegion(id + "F10", true);
            var Q1;
            Q1 = qConstructionFilter(qBodyType(qCreatedBy(id + "F10" ,EDGE), BodyType.WIRE), ConstructionObject.NO);
            extrude(context, id + "F11", {"entities" : qUnion([Q0]), "operationType" : NewBodyOperationType.REMOVE, "surfaceEntities" : qUnion([Q1]), "endBound" : BoundingType.THROUGH_ALL, "oppositeDirection" : true, "depth" : 138.45 * mm, "hasSecondDirection" : true, "secondDirectionOppositeDirection" : false, "secondDirectionDepth" : 25.4 * mm});
        }
        {
            var Q0;
            Q0=qCreatedBy(makeId("Front.planeOp"),FACE);
            var sketch = newSketch(context, id + "F12", { "sketchPlane" : qUnion([Q0])});
            skLineSegment(sketch, "E69.bottom", {"start": v(18.47, -54.17) * mm, "end": v(-10.18, -54.17) * mm});
            skLineSegment(sketch, "E69.top", {"start": v(18.47, -29.22) * mm, "end": v(-10.18, -29.22) * mm});
            skLineSegment(sketch, "E69.left", {"start": v(23.55, -49.09) * mm, "end": v(23.55, -34.3) * mm});
            skLineSegment(sketch, "E69.right", {"start": v(-15.26, -49.09) * mm, "end": v(-15.26, -34.3) * mm});
            skPoint(sketch, "E70.visualSharp", {"position": v(23.55, -54.17) * mm});
            skArc(sketch, "E70.filletArc", {"start": v(18.47, -54.17) * mm, "mid": v(22.07, -52.68) * mm, "end": v(23.55, -49.09) * mm});
            skPoint(sketch, "E71.visualSharp", {"position": v(-15.26, -54.17) * mm});
            skArc(sketch, "E71.filletArc", {"start": v(-15.26, -49.09) * mm, "mid": v(-13.77, -52.68) * mm, "end": v(-10.18, -54.17) * mm});
            skPoint(sketch, "E72.visualSharp", {"position": v(-15.26, -29.22) * mm});
            skArc(sketch, "E72.filletArc", {"start": v(-10.18, -29.22) * mm, "mid": v(-13.77, -30.71) * mm, "end": v(-15.26, -34.3) * mm});
            skPoint(sketch, "E73.visualSharp", {"position": v(23.55, -29.22) * mm});
            skArc(sketch, "E73.filletArc", {"start": v(23.55, -34.3) * mm, "mid": v(22.07, -30.71) * mm, "end": v(18.47, -29.22) * mm});
            skPoint(sketch, "E74.visualSharp", {"position": v(-15.54, 22.76) * mm});
            skPoint(sketch, "E75.visualSharp", {"position": v(7.48, -7.5) * mm});
            skArc(sketch, "E74.filletArc", {"start": v(-10.46, 22.76) * mm, "mid": v(-14.05, 21.27) * mm, "end": v(-15.54, 17.68) * mm});
            skLineSegment(sketch, "E76.right", {"start": v(-15.54, -2.43) * mm, "end": v(-15.54, 17.68) * mm});
            skArc(sketch, "E77.filletArc", {"start": v(-15.54, -2.43) * mm, "mid": v(-14.05, -6.02) * mm, "end": v(-10.46, -7.5) * mm});
            skLineSegment(sketch, "E76.bottom", {"start": v(2.4, -7.5) * mm, "end": v(-10.46, -7.5) * mm});
            skPoint(sketch, "E77.visualSharp", {"position": v(-15.54, -7.5) * mm});
            skPoint(sketch, "E78.visualSharp", {"position": v(7.48, 22.76) * mm});
            skArc(sketch, "E75.filletArc", {"start": v(2.4, -7.5) * mm, "mid": v(5.99, -6.02) * mm, "end": v(7.48, -2.43) * mm});
            skLineSegment(sketch, "E76.left", {"start": v(7.48, -2.43) * mm, "end": v(7.48, 17.68) * mm});
            skLineSegment(sketch, "E76.top", {"start": v(2.4, 22.76) * mm, "end": v(-10.46, 22.76) * mm});
            skArc(sketch, "E78.filletArc", {"start": v(7.48, 17.68) * mm, "mid": v(5.99, 21.27) * mm, "end": v(2.4, 22.76) * mm});
            skArc(sketch, "E79.0", {"start": v(2.4, -4.71) * mm, "mid": v(4.01, -4.04) * mm, "end": v(4.68, -2.43) * mm});
            skLineSegment(sketch, "E79.1", {"start": v(2.4, -4.71) * mm, "end": v(-10.46, -4.71) * mm});
            skLineSegment(sketch, "E79.2", {"start": v(4.68, -2.43) * mm, "end": v(4.68, 17.68) * mm});
            skArc(sketch, "E79.3", {"start": v(-12.75, -2.43) * mm, "mid": v(-12.08, -4.04) * mm, "end": v(-10.46, -4.71) * mm});
            skArc(sketch, "E79.4", {"start": v(4.68, 17.68) * mm, "mid": v(4.01, 19.3) * mm, "end": v(2.4, 19.97) * mm});
            skLineSegment(sketch, "E79.5", {"start": v(2.4, 19.97) * mm, "end": v(-10.46, 19.97) * mm});
            skArc(sketch, "E79.6", {"start": v(-10.46, 19.97) * mm, "mid": v(-12.08, 19.3) * mm, "end": v(-12.75, 17.68) * mm});
            skLineSegment(sketch, "E79.7", {"start": v(-12.75, -2.43) * mm, "end": v(-12.75, 17.68) * mm});
            skLineSegment(sketch, "E80.0", {"start": v(18.47, -31.8) * mm, "end": v(-10.18, -31.8) * mm});
            skArc(sketch, "E80.1", {"start": v(20.99, -34.3) * mm, "mid": v(20.25, -32.53) * mm, "end": v(18.47, -31.8) * mm});
            skArc(sketch, "E80.2", {"start": v(-10.18, -31.8) * mm, "mid": v(-11.96, -32.53) * mm, "end": v(-12.7, -34.3) * mm});
            skLineSegment(sketch, "E80.3", {"start": v(20.99, -49.09) * mm, "end": v(20.99, -34.3) * mm});
            skLineSegment(sketch, "E80.4", {"start": v(-12.7, -49.09) * mm, "end": v(-12.7, -34.3) * mm});
            skArc(sketch, "E80.5", {"start": v(-12.7, -49.09) * mm, "mid": v(-11.96, -50.86) * mm, "end": v(-10.18, -51.6) * mm});
            skLineSegment(sketch, "E80.6", {"start": v(18.47, -51.6) * mm, "end": v(-10.18, -51.6) * mm});
            skArc(sketch, "E80.7", {"start": v(18.47, -51.6) * mm, "mid": v(20.25, -50.86) * mm, "end": v(20.99, -49.09) * mm});
            skSolve(sketch);
        }
        {
            var Q0;
            Q0 = qSketchRegion(id + "F12", true);
            extrude(context, id + "F13", {"entities" : qUnion([Q0]), "operationType" : NewBodyOperationType.ADD, "depth" : 61.75 * mm, "hasSecondDirection" : true, "secondDirectionOppositeDirection" : false, "secondDirectionDepth" : 8.32 * mm});
        }
        {
            var Q0;
            Q0=qCreatedBy(makeId("Top.planeOp"),FACE);
            var sketch = newSketch(context, id + "F14", { "sketchPlane" : qUnion([Q0])});
            skCircle(sketch, "E81", {"center": v(0, 0) * mm, "radius": 26.18 * mm});
            skSolve(sketch);
        }
        {
            var Q0;
            Q0 = qSketchRegion(id + "F14", true);
            extrude(context, id + "F15", {"entities" : qUnion([Q0]), "operationType" : NewBodyOperationType.REMOVE, "depth" : 58.4 * mm, "hasSecondDirection" : true, "secondDirectionOppositeDirection" : true, "secondDirectionDepth" : 93.77 * mm});
        }
        {
            var Q0;
            Q0=makeQuery(id+"F15.boolean.opBoolean","COPY",FACE,{"disambiguationData":[TD([makeQuery(id+"F13.opExtrude","SWEPT_FACE",FACE,{"disambiguationData":[OSD([sQuery(id+"F12.wireOp",EDGE,"E69.bottom")])]})])],"derivedFrom":makeQuery(id+"F15.opExtrude","SWEPT_FACE",FACE,{"disambiguationData":[OSD([sQuery(id+"F14.wireOp",EDGE,"E81")])]})});
            var Q1;
            Q1=makeQuery(id+"F13.opExtrude","CAP_FACE",FACE,{"disambiguationData":[OSD([sQuery(id+"F12.wireOp",EDGE,"E69.bottom"),sQuery(id+"F12.wireOp",EDGE,"E69.top"),sQuery(id+"F12.wireOp",EDGE,"E69.left"),sQuery(id+"F12.wireOp",EDGE,"E69.right"),sQuery(id+"F12.wireOp",EDGE,"E70.filletArc"),sQuery(id+"F12.wireOp",EDGE,"E71.filletArc"),sQuery(id+"F12.wireOp",EDGE,"E72.filletArc"),sQuery(id+"F12.wireOp",EDGE,"E73.filletArc"),sQuery(id+"F12.wireOp",EDGE,"E80.0"),sQuery(id+"F12.wireOp",EDGE,"E80.1"),sQuery(id+"F12.wireOp",EDGE,"E80.2"),sQuery(id+"F12.wireOp",EDGE,"E80.3"),sQuery(id+"F12.wireOp",EDGE,"E80.4"),sQuery(id+"F12.wireOp",EDGE,"E80.5"),sQuery(id+"F12.wireOp",EDGE,"E80.6"),sQuery(id+"F12.wireOp",EDGE,"E80.7")])],"isStart":false});
            var Q2;
            Q2=makeQuery(id+"F13.opExtrude","CAP_FACE",FACE,{"disambiguationData":[OSD([sQuery(id+"F12.wireOp",EDGE,"E74.filletArc"),sQuery(id+"F12.wireOp",EDGE,"E76.right"),sQuery(id+"F12.wireOp",EDGE,"E77.filletArc"),sQuery(id+"F12.wireOp",EDGE,"E76.bottom"),sQuery(id+"F12.wireOp",EDGE,"E75.filletArc"),sQuery(id+"F12.wireOp",EDGE,"E76.left"),sQuery(id+"F12.wireOp",EDGE,"E76.top"),sQuery(id+"F12.wireOp",EDGE,"E78.filletArc"),sQuery(id+"F12.wireOp",EDGE,"E79.0"),sQuery(id+"F12.wireOp",EDGE,"E79.1"),sQuery(id+"F12.wireOp",EDGE,"E79.2"),sQuery(id+"F12.wireOp",EDGE,"E79.3"),sQuery(id+"F12.wireOp",EDGE,"E79.4"),sQuery(id+"F12.wireOp",EDGE,"E79.5"),sQuery(id+"F12.wireOp",EDGE,"E79.6"),sQuery(id+"F12.wireOp",EDGE,"E79.7")])],"isStart":false});
            var Q3;
            Q3=makeQuery(id+"F15.boolean.opBoolean","COPY",FACE,{"disambiguationData":[TD([makeQuery(id+"F13.opExtrude","SWEPT_FACE",FACE,{"disambiguationData":[OSD([sQuery(id+"F12.wireOp",EDGE,"E74.filletArc")])]})])],"derivedFrom":makeQuery(id+"F15.opExtrude","SWEPT_FACE",FACE,{"disambiguationData":[OSD([sQuery(id+"F14.wireOp",EDGE,"E81")])]})});
            chamfer(context, id + "F16", {"entities" : qUnion([Q0, Q1, Q2, Q3]), "width" : 0.76 * mm, "tangentPropagation" : true});
        }
        {
            var Q0;
            {var subQ0=sQuery(id+"F12.wireOp",EDGE,"E69.left");Q0=makeQuery(id+"F16.opChamfer","BLEND_EDGE",EDGE,{"blendedFrom":[makeQuery(id+"F13.opExtrude","CAP_EDGE",EDGE,{"disambiguationData":[OSD([subQ0])],"isStart":false}),makeQuery(id+"F13.opExtrude","CAP_FACE",FACE,{"disambiguationData":[OSD([sQuery(id+"F12.wireOp",EDGE,"E69.bottom"),sQuery(id+"F12.wireOp",EDGE,"E69.top"),subQ0,sQuery(id+"F12.wireOp",EDGE,"E69.right"),sQuery(id+"F12.wireOp",EDGE,"E70.filletArc"),sQuery(id+"F12.wireOp",EDGE,"E71.filletArc"),sQuery(id+"F12.wireOp",EDGE,"E72.filletArc"),sQuery(id+"F12.wireOp",EDGE,"E73.filletArc"),sQuery(id+"F12.wireOp",EDGE,"E80.0"),sQuery(id+"F12.wireOp",EDGE,"E80.1"),sQuery(id+"F12.wireOp",EDGE,"E80.2"),sQuery(id+"F12.wireOp",EDGE,"E80.3"),sQuery(id+"F12.wireOp",EDGE,"E80.4"),sQuery(id+"F12.wireOp",EDGE,"E80.5"),sQuery(id+"F12.wireOp",EDGE,"E80.6"),sQuery(id+"F12.wireOp",EDGE,"E80.7")])],"isStart":false})],"blendedInto":[makeQuery(id+"F13.opExtrude","CAP_FACE",FACE,{"disambiguationData":[OSD([sQuery(id+"F12.wireOp",EDGE,"E69.bottom"),sQuery(id+"F12.wireOp",EDGE,"E69.top"),subQ0,sQuery(id+"F12.wireOp",EDGE,"E69.right"),sQuery(id+"F12.wireOp",EDGE,"E70.filletArc"),sQuery(id+"F12.wireOp",EDGE,"E71.filletArc"),sQuery(id+"F12.wireOp",EDGE,"E72.filletArc"),sQuery(id+"F12.wireOp",EDGE,"E73.filletArc"),sQuery(id+"F12.wireOp",EDGE,"E80.0"),sQuery(id+"F12.wireOp",EDGE,"E80.1"),sQuery(id+"F12.wireOp",EDGE,"E80.2"),sQuery(id+"F12.wireOp",EDGE,"E80.3"),sQuery(id+"F12.wireOp",EDGE,"E80.4"),sQuery(id+"F12.wireOp",EDGE,"E80.5"),sQuery(id+"F12.wireOp",EDGE,"E80.6"),sQuery(id+"F12.wireOp",EDGE,"E80.7")])],"isStart":false})]});}
            var Q1;
            {var subQ0=sQuery(id+"F12.wireOp",EDGE,"E69.left");Q1=makeQuery(id+"F16.opChamfer","BLEND_EDGE",EDGE,{"blendedFrom":[makeQuery(id+"F13.opExtrude","CAP_EDGE",EDGE,{"disambiguationData":[OSD([subQ0])],"isStart":false}),makeQuery(id+"F13.opExtrude","SWEPT_FACE",FACE,{"disambiguationData":[OSD([subQ0])]})],"blendedInto":[makeQuery(id+"F13.opExtrude","SWEPT_FACE",FACE,{"disambiguationData":[OSD([subQ0])]})]});}
            cPlane(context, id + "F17", {"entities" : qUnion([Q0, Q1]), "cplaneType" : CPlaneType.LINE_ANGLE, "offset" : 152.4 * mm, "angle" : 0 * degree, "flipAlignment" : true, "width" : 152.4 * mm, "height" : 152.4 * mm});
        }
        {
            var Q0;
            Q0=qCreatedBy(id+"F17.planeOp",FACE);
            var sketch = newSketch(context, id + "F18", { "sketchPlane" : qUnion([Q0])});
            skLineSegment(sketch, "E82.bottom", {"start": v(21.67, -48.83) * mm, "end": v(50.12, -48.83) * mm});
            skLineSegment(sketch, "E82.top", {"start": v(21.67, -33.55) * mm, "end": v(50.12, -33.55) * mm});
            skLineSegment(sketch, "E82.left", {"start": v(21.67, -48.83) * mm, "end": v(21.67, -33.55) * mm});
            skLineSegment(sketch, "E82.right", {"start": v(50.12, -48.83) * mm, "end": v(50.12, -33.55) * mm});
            skLineSegment(sketch, "E83.bottom", {"start": v(31.91, 6.04) * mm, "end": v(49.95, 6.04) * mm});
            skLineSegment(sketch, "E83.top", {"start": v(31.91, 14.06) * mm, "end": v(49.95, 14.06) * mm});
            skLineSegment(sketch, "E83.left", {"start": v(31.91, 6.04) * mm, "end": v(31.91, 14.06) * mm});
            skLineSegment(sketch, "E83.right", {"start": v(49.95, 6.04) * mm, "end": v(49.95, 14.06) * mm});
            skSolve(sketch);
        }
        {
            var Q0;
            Q0 = qSketchRegion(id + "F18", true);
            extrude(context, id + "F19", {"entities" : qUnion([Q0]), "operationType" : NewBodyOperationType.REMOVE, "depth" : 11.57 * mm});
        }
        {
            var Q0;
            Q0=makeQuery(id+"F13.opExtrude","SWEPT_FACE",FACE,{"disambiguationData":[OSD([sQuery(id+"F12.wireOp",EDGE,"E69.top")])]});
            var sketch = newSketch(context, id + "F20", { "sketchPlane" : qUnion([Q0])});
            skCircle(sketch, "E84", {"center": v(12.79, -50.6) * mm, "radius": 4.1 * mm});
            skCircle(sketch, "E85", {"center": v(6.56, -44.22) * mm, "radius": 2.38 * mm});
            skCircle(sketch, "E86", {"center": v(10.53, -40.13) * mm, "radius": 1.53 * mm});
            skCircle(sketch, "E87", {"center": v(-8.1, -57.73) * mm, "radius": 1.4 * mm});
            skSolve(sketch);
        }
        {
            var Q0;
            Q0 = qSketchRegion(id + "F20", true);
            extrude(context, id + "F21", {"entities" : qUnion([Q0]), "operationType" : NewBodyOperationType.REMOVE, "oppositeDirection" : true, "depth" : 25.4 * mm, "hasSecondDirection" : true, "secondDirectionOppositeDirection" : false, "secondDirectionDepth" : 62.22 * mm});
        }
        {
            var Q0;
            Q0=makeQuery(id+"F13.opExtrude","SWEPT_FACE",FACE,{"disambiguationData":[OSD([sQuery(id+"F12.wireOp",EDGE,"E76.top")])]});
            var sketch = newSketch(context, id + "F22", { "sketchPlane" : qUnion([Q0])});
            skCircle(sketch, "E88", {"center": v(0.95, -59.5) * mm, "radius": 0.71 * mm});
            skCircle(sketch, "E89", {"center": v(-8.87, -59.13) * mm, "radius": 0.71 * mm});
            skCircle(sketch, "E90", {"center": v(-8.84, -47.55) * mm, "radius": 0.71 * mm});
            skCircle(sketch, "E91", {"center": v(0, -40.72) * mm, "radius": 1.93 * mm});
            skSolve(sketch);
        }
        {
            var Q0;
            Q0 = qSketchRegion(id + "F22", true);
            extrude(context, id + "F23", {"entities" : qUnion([Q0]), "operationType" : NewBodyOperationType.REMOVE, "oppositeDirection" : true, "depth" : 38.03 * mm, "hasSecondDirection" : true, "secondDirectionOppositeDirection" : false, "secondDirectionDepth" : 25.4 * mm});
        }
        {
            var Q0;
            Q0=makeQuery(id+"F13.opExtrude","SWEPT_FACE",FACE,{"disambiguationData":[OSD([sQuery(id+"F12.wireOp",EDGE,"E69.bottom")])]});
            var sketch = newSketch(context, id + "F24", { "sketchPlane" : qUnion([Q0])});
            skLineSegment(sketch, "E92.bottom", {"start": v(-18.93, 53.45) * mm, "end": v(-6.13, 53.45) * mm});
            skLineSegment(sketch, "E92.top", {"start": v(-18.93, 51.6) * mm, "end": v(-6.13, 51.6) * mm});
            skLineSegment(sketch, "E92.left", {"start": v(-18.93, 53.45) * mm, "end": v(-18.93, 51.6) * mm});
            skLineSegment(sketch, "E92.right", {"start": v(-6.13, 53.45) * mm, "end": v(-6.13, 51.6) * mm});
            skLineSegment(sketch, "E93.bottom", {"start": v(20.27, 52.18) * mm, "end": v(25, 52.18) * mm});
            skLineSegment(sketch, "E93.top", {"start": v(20.27, 46.56) * mm, "end": v(25, 46.56) * mm});
            skLineSegment(sketch, "E93.left", {"start": v(20.27, 52.18) * mm, "end": v(20.27, 46.56) * mm});
            skLineSegment(sketch, "E93.right", {"start": v(25, 52.18) * mm, "end": v(25, 46.56) * mm});
            skSolve(sketch);
        }
        {
            var Q0;
            Q0 = qSketchRegion(id + "F24", true);
            extrude(context, id + "F25", {"entities" : qUnion([Q0]), "operationType" : NewBodyOperationType.ADD, "oppositeDirection" : true, "depth" : 79 * mm});
        }
    });
